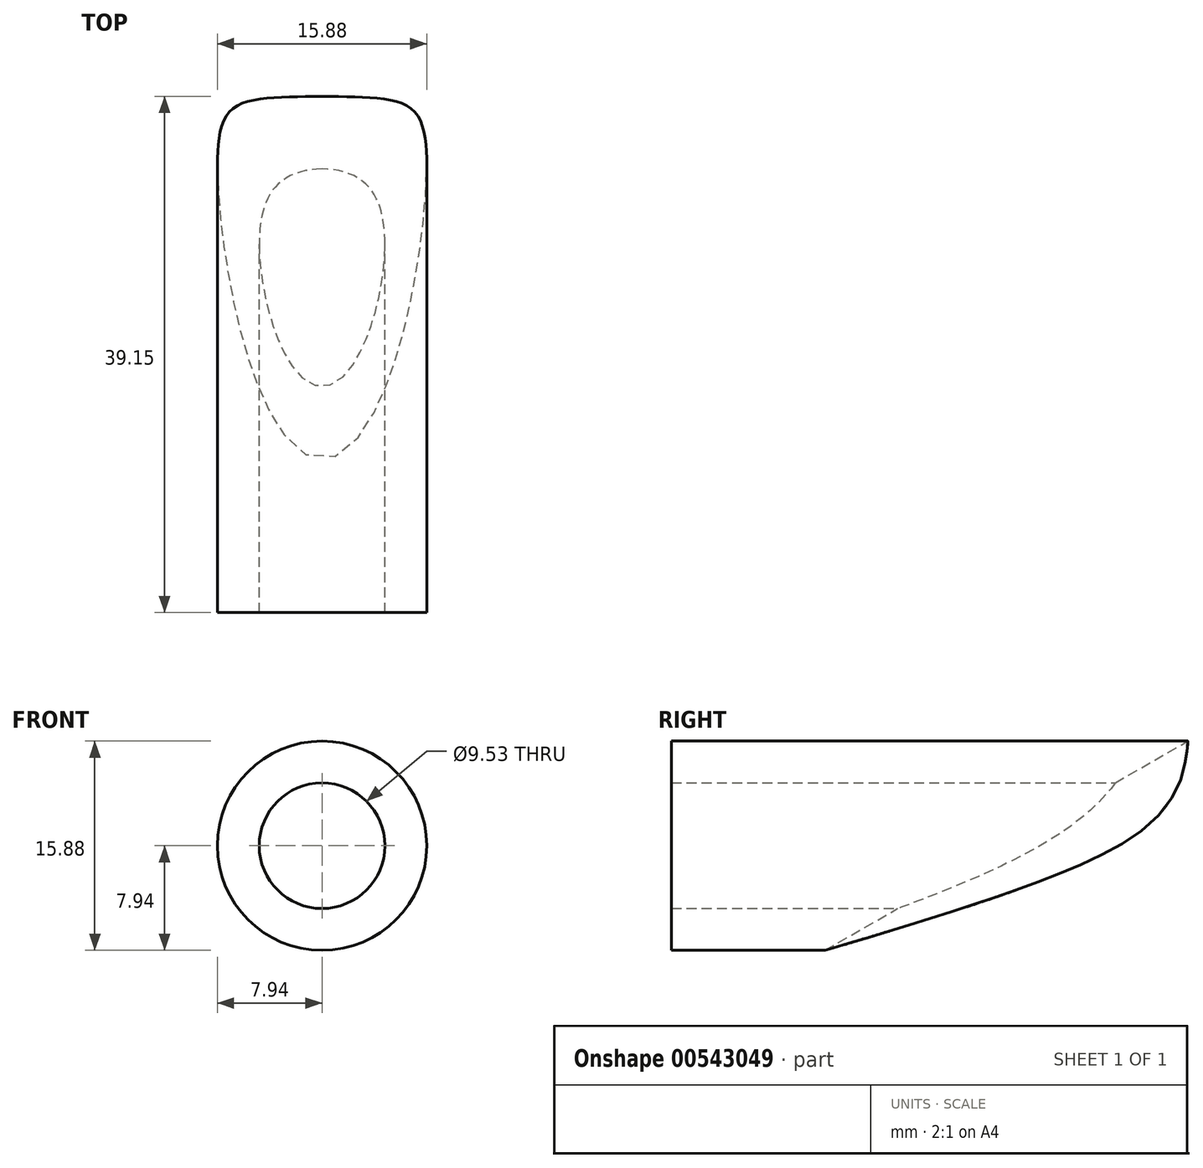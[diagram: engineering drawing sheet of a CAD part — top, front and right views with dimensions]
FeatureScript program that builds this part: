
annotation { "Feature Type Name" : "Feature", "Feature Type Description" : "" }
export const myFeature = defineFeature(function(context is Context, id is Id, definition is map)
    precondition{}
    {
        {
            var Q0;
            Q0=qCreatedBy(makeId("Front.planeOp"),FACE);
            var sketch = newSketch(context, id + "F0", { "sketchPlane" : qUnion([Q0])});
            skCircle(sketch, "E0", {"center": v(0, 0) * mm, "radius": 7.94 * mm});
            skCircle(sketch, "E1", {"center": v(0, 0) * mm, "radius": 4.76 * mm});
            skSolve(sketch);
        }
        {
            var Q0;
            Q0 = qSketchRegion(id + "F0", true);
            extrude(context, id + "F1", {"entities" : qUnion([Q0]), "depth" : 44.45 * mm, "offsetDistance" : 25.4 * mm, "hasSecondDirection" : true, "secondDirectionOppositeDirection" : true, "secondDirectionDepth" : 3.17 * mm});
        }
        {
            var Q0;
            Q0=qCreatedBy(makeId("Front.planeOp"),FACE);
            var sketch = newSketch(context, id + "F2", { "sketchPlane" : qUnion([Q0])});
            skLineSegment(sketch, "E2", {"start": v(-127, 0) * mm, "end": v(127, 0) * mm});
            skLineSegment(sketch, "E3", {"start": v(0, 0) * mm, "end": v(0, -50.8) * mm});
            skSolve(sketch);
        }
        {
            var Q0;
            Q0=sQuery(id+"F2.wireOp",EDGE,"E2");
            var Q1;
            Q1=sQuery(id+"F2.wireOp",EDGE,"E3");
            cPlane(context, id + "F3", {"entities" : qUnion([Q0, Q1]), "cplaneType" : CPlaneType.LINE_ANGLE, "offset" : 25.4 * mm, "angle" : 30 * degree, "width" : 152.4 * mm, "height" : 152.4 * mm});
        }
        {
            var Q0;
            Q0=qCreatedBy(id+"F3.planeOp",FACE);
            var sketch = newSketch(context, id + "F4", { "sketchPlane" : qUnion([Q0])});
            skCircle(sketch, "E4", {"center": v(0, 0) * mm, "radius": 9.53 * mm});
            skSolve(sketch);
        }
        {
            var Q0;
            Q0 = qSketchRegion(id + "F4", true);
            extrude(context, id + "F5", {"entities" : qUnion([Q0]), "operationType" : NewBodyOperationType.REMOVE, "endBound" : BoundingType.THROUGH_ALL, "oppositeDirection" : true, "depth" : 25.4 * mm, "offsetDistance" : 25.4 * mm, "hasSecondDirection" : true, "secondDirectionBound" : SecondDirectionBoundingType.THROUGH_ALL, "secondDirectionOppositeDirection" : false, "secondDirectionDepth" : 25.4 * mm});
        }
    });
